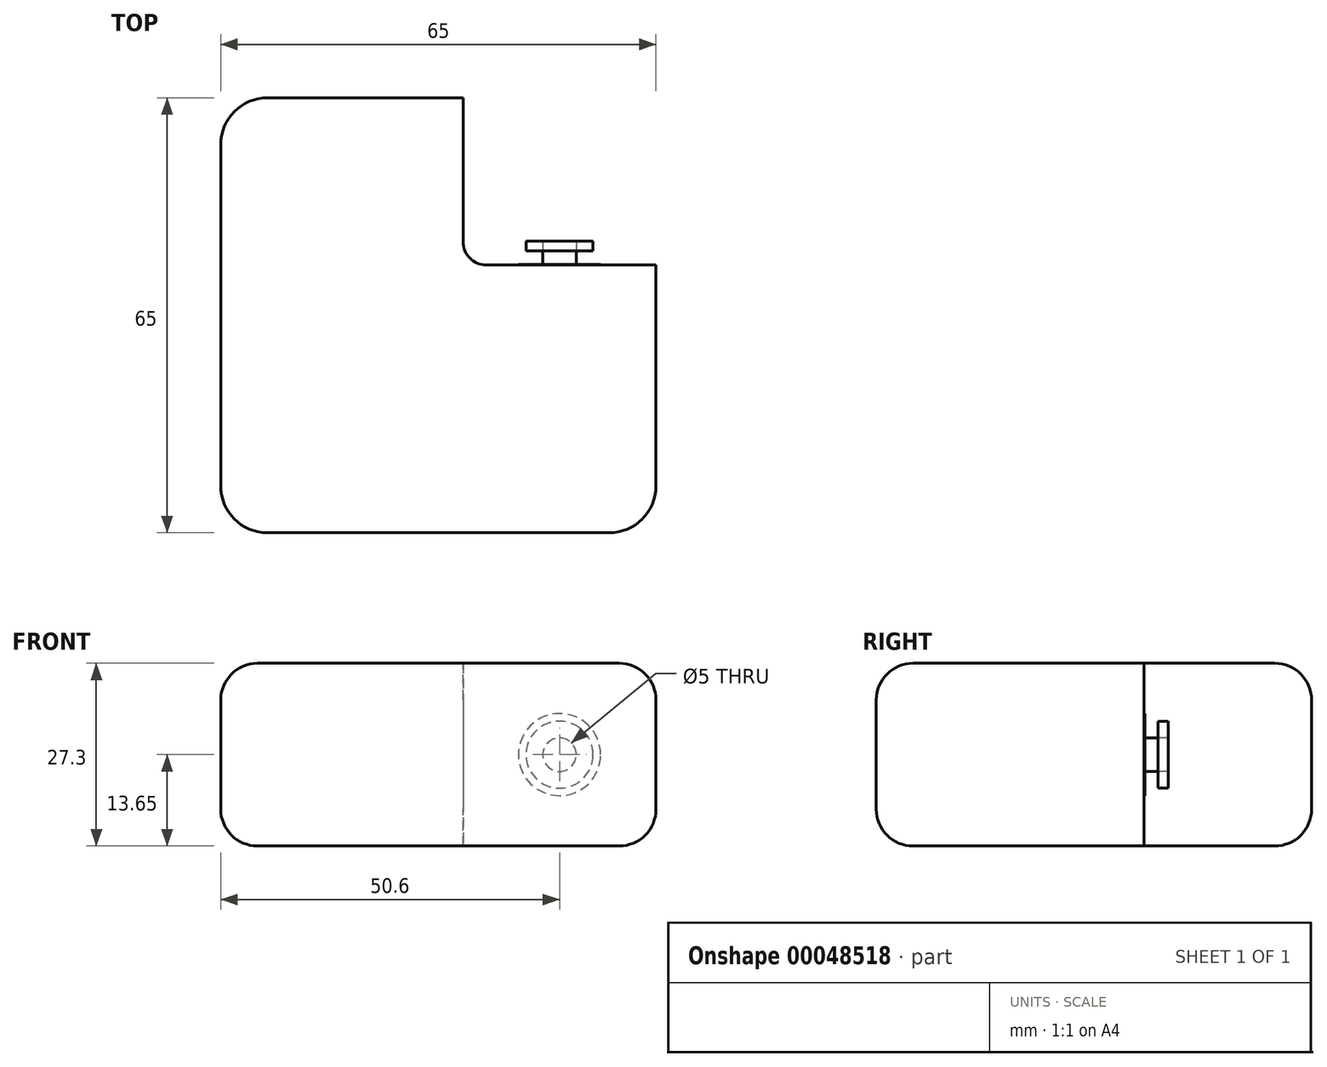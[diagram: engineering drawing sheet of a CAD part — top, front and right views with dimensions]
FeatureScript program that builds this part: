
annotation { "Feature Type Name" : "Feature", "Feature Type Description" : "" }
export const myFeature = defineFeature(function(context is Context, id is Id, definition is map)
    precondition{}
    {
        {
            var Q0;
            Q0=qCreatedBy(makeId("Top.planeOp"),FACE);
            var sketch = newSketch(context, id + "F0", { "sketchPlane" : qUnion([Q0])});
            skLineSegment(sketch, "E0", {"start": v(0, 0) * mm, "end": v(36.2, 0) * mm});
            skLineSegment(sketch, "E1", {"start": v(36.2, 0) * mm, "end": v(36.2, -25) * mm});
            skLineSegment(sketch, "E2", {"start": v(36.2, -25) * mm, "end": v(65, -25) * mm});
            skLineSegment(sketch, "E3", {"start": v(65, -25) * mm, "end": v(65, -65) * mm});
            skLineSegment(sketch, "E4", {"start": v(65, -65) * mm, "end": v(0, -65) * mm});
            skLineSegment(sketch, "E5", {"start": v(0, -65) * mm, "end": v(0, 0) * mm});
            skSolve(sketch);
        }
        {
            var Q0;
            Q0=makeQuery(id+"F0.imprint","IMPRINT",FACE,{"disambiguationData":[TD([[makeQuery(id+"F0.imprint","IMPRINT",EDGE,{"derivedFrom":sQuery(id+"F0.wireOp",EDGE,"E0")}),-1.0]])]});
            extrude(context, id + "F1", {"entities" : qUnion([Q0]), "depth" : 27.3 * mm});
        }
        {
            var Q0;
            Q0=makeQuery(id+"F1.opExtrude","SWEPT_FACE",FACE,{"disambiguationData":[OSD([sQuery(id+"F0.wireOp",EDGE,"E2")])]});
            var sketch = newSketch(context, id + "F2", { "sketchPlane" : qUnion([Q0])});
            skCircle(sketch, "E6", {"center": v(-50.6, 13.65) * mm, "radius": 6.13 * mm});
            skLineSegment(sketch, "E7", {"start": v(-65, 0) * mm, "end": v(-36.2, 27.3) * mm, "construction": true});
            skSolve(sketch);
        }
        {
            var Q0;
            Q0=makeQuery(id+"F1.opExtrude","SWEPT_EDGE",EDGE,{"disambiguationData":[OSD([sQuery(id+"F0.wireOp",EDGE,"E0"),sQuery(id+"F0.wireOp",EDGE,"E5")])]});
            var Q1;
            Q1=makeQuery(id+"F1.opExtrude","SWEPT_EDGE",EDGE,{"disambiguationData":[OSD([sQuery(id+"F0.wireOp",EDGE,"E4"),sQuery(id+"F0.wireOp",EDGE,"E5")])]});
            var Q2;
            Q2=makeQuery(id+"F1.opExtrude","SWEPT_EDGE",EDGE,{"disambiguationData":[OSD([sQuery(id+"F0.wireOp",EDGE,"E3"),sQuery(id+"F0.wireOp",EDGE,"E4")])]});
            fillet(context, id + "F3", {"entities" : qUnion([Q0, Q1, Q2]), "radius" : 7 * mm, "tangentPropagation" : true, "allowEdgeOverflow" : false});
        }
        {
            var Q0;
            Q0=makeQuery(id+"F1.opExtrude","SWEPT_EDGE",EDGE,{"disambiguationData":[OSD([sQuery(id+"F0.wireOp",EDGE,"E1"),sQuery(id+"F0.wireOp",EDGE,"E2")])]});
            fillet(context, id + "F4", {"entities" : qUnion([Q0]), "radius" : 3.5 * mm, "tangentPropagation" : true, "allowEdgeOverflow" : false});
        }
        {
            var Q0;
            Q0=makeQuery(id+"F1.opExtrude","CAP_EDGE",EDGE,{"disambiguationData":[OSD([sQuery(id+"F0.wireOp",EDGE,"E3")])],"isStart":true});
            var Q1;
            {var subQ0=sQuery(id+"F0.wireOp",EDGE,"E3");var subQ1=sQuery(id+"F0.wireOp",EDGE,"E4");Q1=makeQuery(id+"F3.opFillet","BLEND_EDGE",EDGE,{"blendedFrom":[makeQuery(id+"F1.opExtrude","SWEPT_EDGE",EDGE,{"disambiguationData":[OSD([subQ0,subQ1])]}),makeQuery(id+"F1.opExtrude","CAP_FACE",FACE,{"disambiguationData":[OSD([sQuery(id+"F0.wireOp",EDGE,"E0"),sQuery(id+"F0.wireOp",EDGE,"E1"),sQuery(id+"F0.wireOp",EDGE,"E2"),subQ0,subQ1,sQuery(id+"F0.wireOp",EDGE,"E5")])],"isStart":true})],"blendedInto":[makeQuery(id+"F1.opExtrude","CAP_FACE",FACE,{"disambiguationData":[OSD([sQuery(id+"F0.wireOp",EDGE,"E0"),sQuery(id+"F0.wireOp",EDGE,"E1"),sQuery(id+"F0.wireOp",EDGE,"E2"),subQ0,subQ1,sQuery(id+"F0.wireOp",EDGE,"E5")])],"isStart":true})]});}
            var Q2;
            Q2=makeQuery(id+"F1.opExtrude","CAP_EDGE",EDGE,{"disambiguationData":[OSD([sQuery(id+"F0.wireOp",EDGE,"E4")])],"isStart":true});
            var Q3;
            {var subQ0=sQuery(id+"F0.wireOp",EDGE,"E4");var subQ1=sQuery(id+"F0.wireOp",EDGE,"E5");Q3=makeQuery(id+"F3.opFillet","BLEND_EDGE",EDGE,{"blendedFrom":[makeQuery(id+"F1.opExtrude","SWEPT_EDGE",EDGE,{"disambiguationData":[OSD([subQ0,subQ1])]}),makeQuery(id+"F1.opExtrude","CAP_FACE",FACE,{"disambiguationData":[OSD([sQuery(id+"F0.wireOp",EDGE,"E0"),sQuery(id+"F0.wireOp",EDGE,"E1"),sQuery(id+"F0.wireOp",EDGE,"E2"),sQuery(id+"F0.wireOp",EDGE,"E3"),subQ0,subQ1])],"isStart":true})],"blendedInto":[makeQuery(id+"F1.opExtrude","CAP_FACE",FACE,{"disambiguationData":[OSD([sQuery(id+"F0.wireOp",EDGE,"E0"),sQuery(id+"F0.wireOp",EDGE,"E1"),sQuery(id+"F0.wireOp",EDGE,"E2"),sQuery(id+"F0.wireOp",EDGE,"E3"),subQ0,subQ1])],"isStart":true})]});}
            var Q4;
            Q4=makeQuery(id+"F1.opExtrude","CAP_EDGE",EDGE,{"disambiguationData":[OSD([sQuery(id+"F0.wireOp",EDGE,"E5")])],"isStart":true});
            var Q5;
            {var subQ0=sQuery(id+"F0.wireOp",EDGE,"E0");var subQ1=sQuery(id+"F0.wireOp",EDGE,"E5");Q5=makeQuery(id+"F3.opFillet","BLEND_EDGE",EDGE,{"blendedFrom":[makeQuery(id+"F1.opExtrude","SWEPT_EDGE",EDGE,{"disambiguationData":[OSD([subQ0,subQ1])]}),makeQuery(id+"F1.opExtrude","CAP_FACE",FACE,{"disambiguationData":[OSD([subQ0,sQuery(id+"F0.wireOp",EDGE,"E1"),sQuery(id+"F0.wireOp",EDGE,"E2"),sQuery(id+"F0.wireOp",EDGE,"E3"),sQuery(id+"F0.wireOp",EDGE,"E4"),subQ1])],"isStart":true})],"blendedInto":[makeQuery(id+"F1.opExtrude","CAP_FACE",FACE,{"disambiguationData":[OSD([subQ0,sQuery(id+"F0.wireOp",EDGE,"E1"),sQuery(id+"F0.wireOp",EDGE,"E2"),sQuery(id+"F0.wireOp",EDGE,"E3"),sQuery(id+"F0.wireOp",EDGE,"E4"),subQ1])],"isStart":true})]});}
            var Q6;
            Q6=makeQuery(id+"F1.opExtrude","CAP_EDGE",EDGE,{"disambiguationData":[OSD([sQuery(id+"F0.wireOp",EDGE,"E0")])],"isStart":true});
            var Q7;
            Q7=makeQuery(id+"F1.opExtrude","CAP_EDGE",EDGE,{"disambiguationData":[OSD([sQuery(id+"F0.wireOp",EDGE,"E0")])],"isStart":false});
            var Q8;
            {var subQ0=sQuery(id+"F0.wireOp",EDGE,"E0");var subQ1=sQuery(id+"F0.wireOp",EDGE,"E5");Q8=makeQuery(id+"F3.opFillet","BLEND_EDGE",EDGE,{"blendedFrom":[makeQuery(id+"F1.opExtrude","SWEPT_EDGE",EDGE,{"disambiguationData":[OSD([subQ0,subQ1])]}),makeQuery(id+"F1.opExtrude","CAP_FACE",FACE,{"disambiguationData":[OSD([subQ0,sQuery(id+"F0.wireOp",EDGE,"E1"),sQuery(id+"F0.wireOp",EDGE,"E2"),sQuery(id+"F0.wireOp",EDGE,"E3"),sQuery(id+"F0.wireOp",EDGE,"E4"),subQ1])],"isStart":false})],"blendedInto":[makeQuery(id+"F1.opExtrude","CAP_FACE",FACE,{"disambiguationData":[OSD([subQ0,sQuery(id+"F0.wireOp",EDGE,"E1"),sQuery(id+"F0.wireOp",EDGE,"E2"),sQuery(id+"F0.wireOp",EDGE,"E3"),sQuery(id+"F0.wireOp",EDGE,"E4"),subQ1])],"isStart":false})]});}
            var Q9;
            Q9=makeQuery(id+"F1.opExtrude","CAP_EDGE",EDGE,{"disambiguationData":[OSD([sQuery(id+"F0.wireOp",EDGE,"E5")])],"isStart":false});
            var Q10;
            {var subQ0=sQuery(id+"F0.wireOp",EDGE,"E4");var subQ1=sQuery(id+"F0.wireOp",EDGE,"E5");Q10=makeQuery(id+"F3.opFillet","BLEND_EDGE",EDGE,{"blendedFrom":[makeQuery(id+"F1.opExtrude","SWEPT_EDGE",EDGE,{"disambiguationData":[OSD([subQ0,subQ1])]}),makeQuery(id+"F1.opExtrude","CAP_FACE",FACE,{"disambiguationData":[OSD([sQuery(id+"F0.wireOp",EDGE,"E0"),sQuery(id+"F0.wireOp",EDGE,"E1"),sQuery(id+"F0.wireOp",EDGE,"E2"),sQuery(id+"F0.wireOp",EDGE,"E3"),subQ0,subQ1])],"isStart":false})],"blendedInto":[makeQuery(id+"F1.opExtrude","CAP_FACE",FACE,{"disambiguationData":[OSD([sQuery(id+"F0.wireOp",EDGE,"E0"),sQuery(id+"F0.wireOp",EDGE,"E1"),sQuery(id+"F0.wireOp",EDGE,"E2"),sQuery(id+"F0.wireOp",EDGE,"E3"),subQ0,subQ1])],"isStart":false})]});}
            var Q11;
            Q11=makeQuery(id+"F1.opExtrude","CAP_EDGE",EDGE,{"disambiguationData":[OSD([sQuery(id+"F0.wireOp",EDGE,"E4")])],"isStart":false});
            var Q12;
            {var subQ0=sQuery(id+"F0.wireOp",EDGE,"E3");var subQ1=sQuery(id+"F0.wireOp",EDGE,"E4");Q12=makeQuery(id+"F3.opFillet","BLEND_EDGE",EDGE,{"blendedFrom":[makeQuery(id+"F1.opExtrude","SWEPT_EDGE",EDGE,{"disambiguationData":[OSD([subQ0,subQ1])]}),makeQuery(id+"F1.opExtrude","CAP_FACE",FACE,{"disambiguationData":[OSD([sQuery(id+"F0.wireOp",EDGE,"E0"),sQuery(id+"F0.wireOp",EDGE,"E1"),sQuery(id+"F0.wireOp",EDGE,"E2"),subQ0,subQ1,sQuery(id+"F0.wireOp",EDGE,"E5")])],"isStart":false})],"blendedInto":[makeQuery(id+"F1.opExtrude","CAP_FACE",FACE,{"disambiguationData":[OSD([sQuery(id+"F0.wireOp",EDGE,"E0"),sQuery(id+"F0.wireOp",EDGE,"E1"),sQuery(id+"F0.wireOp",EDGE,"E2"),subQ0,subQ1,sQuery(id+"F0.wireOp",EDGE,"E5")])],"isStart":false})]});}
            var Q13;
            Q13=makeQuery(id+"F1.opExtrude","CAP_EDGE",EDGE,{"disambiguationData":[OSD([sQuery(id+"F0.wireOp",EDGE,"E3")])],"isStart":false});
            fillet(context, id + "F5", {"entities" : qUnion([Q0, Q1, Q2, Q3, Q4, Q5, Q6, Q7, Q8, Q9, Q10, Q11, Q12, Q13]), "radius" : 5.5 * mm, "tangentPropagation" : true, "allowEdgeOverflow" : false});
        }
        {
            var Q0;
            Q0=makeQuery(id+"F2.imprint","IMPRINT",FACE,{"disambiguationData":[TD([[makeQuery(id+"F2.imprint","IMPRINT",EDGE,{"derivedFrom":sQuery(id+"F2.wireOp",EDGE,"E6")}),1.0]])]});
            extrude(context, id + "F6", {"entities" : qUnion([Q0]), "operationType" : NewBodyOperationType.ADD, "depth" : 0.1 * mm});
        }
        {
            var Q0;
            Q0=makeQuery(id+"F6.opExtrude","CAP_FACE",FACE,{"disambiguationData":[OSD([sQuery(id+"F2.wireOp",EDGE,"E6")])],"isStart":false});
            var sketch = newSketch(context, id + "F7", { "sketchPlane" : qUnion([Q0])});
            skCircle(sketch, "E8", {"center": v(-50.6, 13.65) * mm, "radius": 2.5 * mm});
            skSolve(sketch);
        }
        {
            var Q0;
            Q0=makeQuery(id+"F7.imprint","IMPRINT",FACE,{"disambiguationData":[TD([[makeQuery(id+"F7.imprint","IMPRINT",EDGE,{"derivedFrom":sQuery(id+"F7.wireOp",EDGE,"E8")}),1.0]])]});
            extrude(context, id + "F8", {"entities" : qUnion([Q0]), "operationType" : NewBodyOperationType.ADD, "depth" : 2 * mm});
        }
        {
            var Q0;
            Q0=makeQuery(id+"F8.opExtrude","CAP_FACE",FACE,{"disambiguationData":[OSD([sQuery(id+"F7.wireOp",EDGE,"E8")])],"isStart":false});
            var sketch = newSketch(context, id + "F9", { "sketchPlane" : qUnion([Q0])});
            skCircle(sketch, "E9", {"center": v(-50.6, 13.65) * mm, "radius": 5 * mm});
            skSolve(sketch);
        }
        {
            var Q0;
            Q0=makeQuery(id+"F9.imprint","IMPRINT",FACE,{"disambiguationData":[TD([[makeQuery(id+"F9.imprint","IMPRINT",EDGE,{"derivedFrom":sQuery(id+"F9.wireOp",EDGE,"E9")}),1.0]])]});
            extrude(context, id + "F10", {"entities" : qUnion([Q0]), "depth" : 1.5 * mm});
        }
    });
